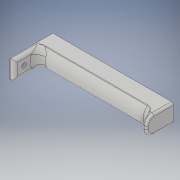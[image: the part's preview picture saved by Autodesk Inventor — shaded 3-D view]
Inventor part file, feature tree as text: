
AUTODESK INVENTOR PART (.ipt)
format: ipt  version: 2018 (Build 220112000, 112)  size: 353,280 bytes
history: native  units: in
note: dims shown in document units (in); Inventor stores cm internally (conversion verified against a paired STEP export)
features: extrude x7, sketch x7, projected_geometry x7, fillet x5, chamfer x1
ambient origin geometry x8: Origin, YZ Plane, XZ Plane, XY Plane, X Axis, Y Axis, Z Axis, Center Point
bodies: Solid1 (feature_tree)
feature tree (27):
  extrude  "Extrusion1"  Depth=0.5512in
  extrude  "Extrusion2"  Depth=1.5748in TaperAngle=0.0deg
  fillet  "Fillet3"  Radius=1.5748in
  fillet  "Fillet4"  Radius=0.1575in
  extrude  "Extrusion3"  Depth=0.1181in
  extrude  "Extrusion4"  Depth=0.1181in TaperAngle=0.0deg
  fillet  "Fillet5"  Radius=0.9843in
  fillet  "Fillet6"  Radius=0.1181in
  fillet  "Fillet7"  Radius=0.2756in
  extrude  "Extrusion5"  Depth=0.0394in
  chamfer  "Chamfer1"  Distance=0.1181in
  extrude  "Extrusion6"  Depth=0.1181in TaperAngle=45.0deg
  extrude  "Extrusion7"  Depth=0.1181in
  sketch  "Sketch1"  dims[d1=0.6693in d2=0.5512in]
  sketch  "Sketch2"  dims[d3=0.4331in d4=4.1339in d5=0.0in d6=1.5748in d7=0.1575in d8=0.0in]
  sketch  "Sketch3"  dims[d11=0.1181in d12=0.2756in]
  sketch  "Sketch4"  dims[d13=0.1654in d14=0.1575in d15=0.0in d16=0.9843in d17=0.1181in d18=0.0in d19=0.2756in]
  sketch  "Sketch5"  dims[d20=0.0787in d21=0.0394in]
  sketch  "Sketch6"  dims[d22=0.1969in]
  projected_geometry  "Projected Loop1"
  projected_geometry  "Projected Loop2"
  projected_geometry  "Projected Loop3"
  projected_geometry  "Projected Loop4"
  projected_geometry  "Projected Loop5"
  projected_geometry  "Projected Loop6"
  sketch  "Sketch7"  dims[d23=0.3937in d24=0.1181in d25=0.0in d26=0.0787in d27=0.0787in d28=45.0deg d29=0.1969in d31=0.5512in d32=0.4331in d33=4.1339in d34=0.0in d35=0.1181in d36=0.0in]
  projected_geometry  "Projected Loop7"
